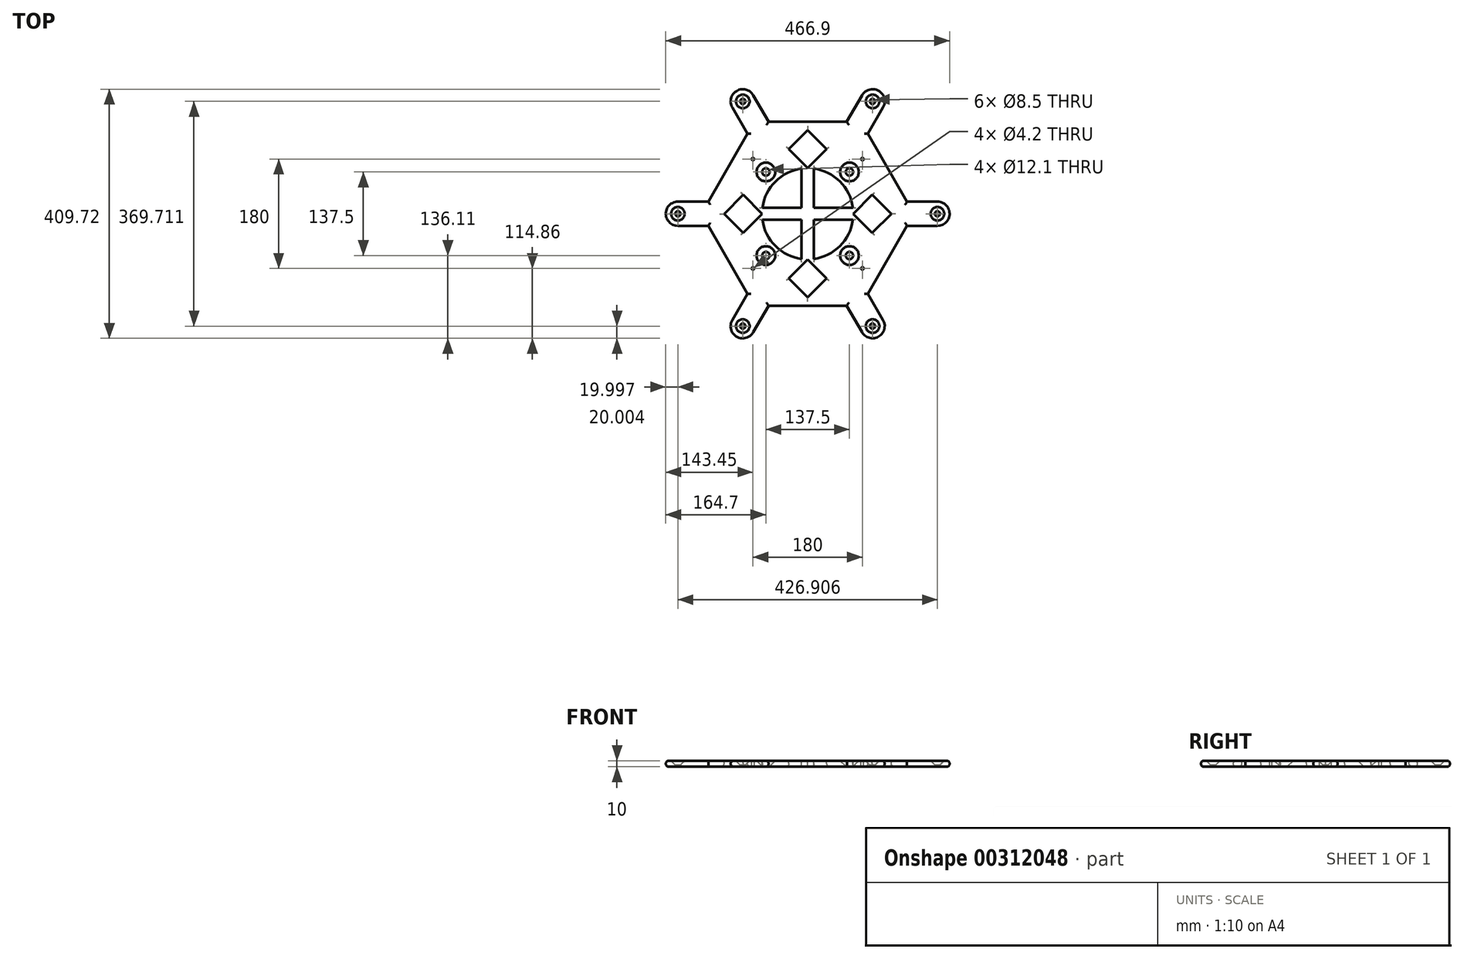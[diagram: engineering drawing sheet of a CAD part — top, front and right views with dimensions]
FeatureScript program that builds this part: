
annotation { "Feature Type Name" : "Feature", "Feature Type Description" : "" }
export const myFeature = defineFeature(function(context is Context, id is Id, definition is map)
    precondition{}
    {
        {
            var Q0;
            Q0=qCreatedBy(makeId("Top.planeOp"),FACE);
            var sketch = newSketch(context, id + "F0", { "sketchPlane" : qUnion([Q0])});
            skCircle(sketch, "E0.cCircle", {"center": v(0, 0) * mm, "radius": 175 * mm, "construction": true});
            skLineSegment(sketch, "E0.0", {"start": v(-87.5, 151.55) * mm, "end": v(87.5, 151.55) * mm});
            skLineSegment(sketch, "E0.1", {"start": v(87.5, 151.55) * mm, "end": v(175, 0) * mm});
            skLineSegment(sketch, "E0.2", {"start": v(175, 0) * mm, "end": v(87.5, -151.55) * mm});
            skLineSegment(sketch, "E0.3", {"start": v(87.5, -151.55) * mm, "end": v(-87.5, -151.55) * mm});
            skLineSegment(sketch, "E0.4", {"start": v(-87.5, -151.55) * mm, "end": v(-175, 0) * mm});
            skLineSegment(sketch, "E0.5", {"start": v(-175, 0) * mm, "end": v(-87.5, 151.55) * mm});
            skLineSegment(sketch, "E1.bottom", {"start": v(-213.45, 20) * mm, "end": v(-163.45, 20) * mm});
            skLineSegment(sketch, "E1.top", {"start": v(-213.45, -20) * mm, "end": v(-163.45, -20) * mm});
            skLineSegment(sketch, "E1.left", {"start": v(-213.45, 20) * mm, "end": v(-213.45, -20) * mm});
            skPoint(sketch, "E2.startSnap0", {"position": v(0, 151.55) * mm});
            skPoint(sketch, "E2.endSnap0", {"position": v(0, -151.55) * mm});
            skLineSegment(sketch, "E3", {"start": v(-175, 0) * mm, "end": v(-213.45, 0) * mm, "construction": true});
            skLineSegment(sketch, "E4.1.0", {"start": v(-124.05, -174.86) * mm, "end": v(-89.4, -194.86) * mm});
            skLineSegment(sketch, "E4.1.1", {"start": v(-124.05, -174.86) * mm, "end": v(-99.05, -131.55) * mm});
            skLineSegment(sketch, "E4.1.2", {"start": v(-89.4, -194.86) * mm, "end": v(-64.4, -151.55) * mm});
            skLineSegment(sketch, "E4.2.0", {"start": v(89.4, -194.86) * mm, "end": v(124.05, -174.86) * mm});
            skLineSegment(sketch, "E4.2.1", {"start": v(89.4, -194.86) * mm, "end": v(64.4, -151.55) * mm});
            skLineSegment(sketch, "E4.2.2", {"start": v(124.05, -174.86) * mm, "end": v(99.05, -131.55) * mm});
            skLineSegment(sketch, "E4.3.0", {"start": v(213.45, -20) * mm, "end": v(213.45, 20) * mm});
            skLineSegment(sketch, "E4.3.1", {"start": v(213.45, -20) * mm, "end": v(163.45, -20) * mm});
            skLineSegment(sketch, "E4.3.2", {"start": v(213.45, 20) * mm, "end": v(163.45, 20) * mm});
            skLineSegment(sketch, "E4.4.0", {"start": v(124.05, 174.86) * mm, "end": v(89.4, 194.86) * mm});
            skLineSegment(sketch, "E4.4.1", {"start": v(124.05, 174.86) * mm, "end": v(99.05, 131.55) * mm});
            skLineSegment(sketch, "E4.4.2", {"start": v(89.4, 194.86) * mm, "end": v(64.4, 151.55) * mm});
            skLineSegment(sketch, "E4.5.0", {"start": v(-89.4, 194.86) * mm, "end": v(-124.05, 174.86) * mm});
            skLineSegment(sketch, "E4.5.1", {"start": v(-89.4, 194.86) * mm, "end": v(-64.4, 151.55) * mm});
            skLineSegment(sketch, "E4.5.2", {"start": v(-124.05, 174.86) * mm, "end": v(-99.05, 131.55) * mm});
            skArc(sketch, "E5", {"start": v(-213.45, 20) * mm, "mid": v(-233.45, 0) * mm, "end": v(-213.45, -20) * mm});
            skArc(sketch, "E6.1.0", {"start": v(-124.05, -174.86) * mm, "mid": v(-116.73, -202.18) * mm, "end": v(-89.4, -194.86) * mm});
            skArc(sketch, "E6.2.0", {"start": v(89.4, -194.86) * mm, "mid": v(116.73, -202.18) * mm, "end": v(124.05, -174.86) * mm});
            skArc(sketch, "E6.3.0", {"start": v(213.45, -20) * mm, "mid": v(233.45, 0) * mm, "end": v(213.45, 20) * mm});
            skArc(sketch, "E6.4.0", {"start": v(124.05, 174.86) * mm, "mid": v(116.73, 202.18) * mm, "end": v(89.4, 194.86) * mm});
            skArc(sketch, "E6.5.0", {"start": v(-89.4, 194.86) * mm, "mid": v(-116.73, 202.18) * mm, "end": v(-124.05, 174.86) * mm});
            skSolve(sketch);
        }
        {
            var Q0;
            Q0 = qSketchRegion(id + "F0", true);
            extrude(context, id + "F1", {"entities" : qUnion([Q0]), "depth" : 10 * mm});
        }
        {
            var Q0;
            Q0=makeQuery(id+"F1.opExtrude","CAP_FACE",FACE,{"disambiguationData":[OSD([sQuery(id+"F0.wireOp",EDGE,"E0.0"),sQuery(id+"F0.wireOp",EDGE,"E0.1"),sQuery(id+"F0.wireOp",EDGE,"E0.2"),sQuery(id+"F0.wireOp",EDGE,"E0.3"),sQuery(id+"F0.wireOp",EDGE,"E0.4"),sQuery(id+"F0.wireOp",EDGE,"E0.5"),sQuery(id+"F0.wireOp",EDGE,"E1.bottom"),sQuery(id+"F0.wireOp",EDGE,"E1.top"),sQuery(id+"F0.wireOp",EDGE,"E4.1.1"),sQuery(id+"F0.wireOp",EDGE,"E4.1.2"),sQuery(id+"F0.wireOp",EDGE,"E4.2.1"),sQuery(id+"F0.wireOp",EDGE,"E4.2.2"),sQuery(id+"F0.wireOp",EDGE,"E4.3.1"),sQuery(id+"F0.wireOp",EDGE,"E4.3.2"),sQuery(id+"F0.wireOp",EDGE,"E4.4.1"),sQuery(id+"F0.wireOp",EDGE,"E4.4.2"),sQuery(id+"F0.wireOp",EDGE,"E4.5.1"),sQuery(id+"F0.wireOp",EDGE,"E4.5.2"),sQuery(id+"F0.wireOp",EDGE,"E5"),sQuery(id+"F0.wireOp",EDGE,"E6.1.0"),sQuery(id+"F0.wireOp",EDGE,"E6.2.0"),sQuery(id+"F0.wireOp",EDGE,"E6.3.0"),sQuery(id+"F0.wireOp",EDGE,"E6.4.0"),sQuery(id+"F0.wireOp",EDGE,"E6.5.0")])],"isStart":false});
            var sketch = newSketch(context, id + "F2", { "sketchPlane" : qUnion([Q0])});
            skCircle(sketch, "E7", {"center": v(0, 0) * mm, "radius": 137.5 * mm});
            skCircle(sketch, "E8", {"center": v(0, 0) * mm, "radius": 75 * mm});
            skLineSegment(sketch, "E9", {"start": v(137.5, 0) * mm, "end": v(0, 137.5) * mm});
            skLineSegment(sketch, "E10", {"start": v(0, 137.5) * mm, "end": v(-137.5, 0) * mm});
            skLineSegment(sketch, "E11", {"start": v(-137.5, 0) * mm, "end": v(0, -137.5) * mm});
            skLineSegment(sketch, "E12", {"start": v(0, -137.5) * mm, "end": v(137.5, 0) * mm});
            skLineSegment(sketch, "E13", {"start": v(-75, 0) * mm, "end": v(-106.25, 31.25) * mm});
            skLineSegment(sketch, "E14", {"start": v(0, 75) * mm, "end": v(-31.25, 106.25) * mm});
            skLineSegment(sketch, "E15", {"start": v(0, 75) * mm, "end": v(31.25, 106.25) * mm});
            skLineSegment(sketch, "E16", {"start": v(-75, 0) * mm, "end": v(-106.25, -31.25) * mm});
            skLineSegment(sketch, "E17", {"start": v(0, -75) * mm, "end": v(-31.25, -106.25) * mm});
            skLineSegment(sketch, "E18", {"start": v(0, -75) * mm, "end": v(31.25, -106.25) * mm});
            skLineSegment(sketch, "E19", {"start": v(75, 0) * mm, "end": v(106.25, 31.25) * mm});
            skLineSegment(sketch, "E20", {"start": v(75, 0) * mm, "end": v(106.25, -31.25) * mm});
            skLineSegment(sketch, "E21", {"start": v(0, 75) * mm, "end": v(0, -75) * mm, "construction": true});
            skLineSegment(sketch, "E22", {"start": v(-75, 0) * mm, "end": v(75, 0) * mm, "construction": true});
            skLineSegment(sketch, "E23", {"start": v(-10, 74.33) * mm, "end": v(-10, -74.33) * mm});
            skLineSegment(sketch, "E24", {"start": v(10, 74.33) * mm, "end": v(10, -74.33) * mm});
            skLineSegment(sketch, "E25", {"start": v(-74.33, 10) * mm, "end": v(74.33, 10) * mm});
            skLineSegment(sketch, "E26", {"start": v(74.33, -10) * mm, "end": v(-74.33, -10) * mm});
            skLineSegment(sketch, "E27", {"start": v(-68.75, 68.75) * mm, "end": v(68.75, -68.75) * mm, "construction": true});
            skLineSegment(sketch, "E28", {"start": v(-68.75, -68.75) * mm, "end": v(68.75, 68.75) * mm, "construction": true});
            skPoint(sketch, "E29", {"position": v(-68.75, 68.75) * mm});
            skPoint(sketch, "E30", {"position": v(68.75, 68.75) * mm});
            skPoint(sketch, "E31", {"position": v(-68.75, -68.75) * mm});
            skPoint(sketch, "E32", {"position": v(68.75, -68.75) * mm});
            skSolve(sketch);
        }
        {
            var Q0;
            {var subQ3=sQuery(id+"F2.wireOp",EDGE,"E13");Q0=makeQuery(id+"F2.imprint","IMPRINT",FACE,{"disambiguationData":[TD([[makeQuery(id+"F2.imprint","IMPRINT",EDGE,{"derivedFrom":subQ3}),1.0]])]});}
            var Q1;
            {var subQ4=sQuery(id+"F2.wireOp",EDGE,"E14");Q1=makeQuery(id+"F2.imprint","IMPRINT",FACE,{"disambiguationData":[TD([[makeQuery(id+"F2.imprint","IMPRINT",EDGE,{"derivedFrom":subQ4}),-1.0]])]});}
            var Q2;
            {var subQ3=sQuery(id+"F2.wireOp",EDGE,"E19");Q2=makeQuery(id+"F2.imprint","IMPRINT",FACE,{"disambiguationData":[TD([[makeQuery(id+"F2.imprint","IMPRINT",EDGE,{"derivedFrom":subQ3}),-1.0]])]});}
            var Q3;
            {var subQ3=sQuery(id+"F2.wireOp",EDGE,"E17");Q3=makeQuery(id+"F2.imprint","IMPRINT",FACE,{"disambiguationData":[TD([[makeQuery(id+"F2.imprint","IMPRINT",EDGE,{"derivedFrom":subQ3}),1.0]])]});}
            var Q4;
            {var subQ0=sQuery(id+"F2.wireOp",EDGE,"E24");var subQ1=sQuery(id+"F2.wireOp",EDGE,"E8");var subQ2=makeQuery(id+"F2.imprint","INTERSECT",VERTEX,{"disambiguationData":[OD(1.0)],"derivedFrom":[subQ1,subQ0]});Q4=makeQuery(id+"F2.imprint","IMPRINT",FACE,{"disambiguationData":[TD([[makeQuery(id+"F2.imprint","IMPRINT",EDGE,{"disambiguationData":[TD([[subQ2,-1.0]])],"derivedFrom":subQ1}),1.0]])]});}
            var Q5;
            {var subQ0=sQuery(id+"F2.wireOp",EDGE,"E23");var subQ1=sQuery(id+"F2.wireOp",EDGE,"E8");var subQ2=makeQuery(id+"F2.imprint","INTERSECT",VERTEX,{"disambiguationData":[OD(1.0)],"derivedFrom":[subQ1,subQ0]});Q5=makeQuery(id+"F2.imprint","IMPRINT",FACE,{"disambiguationData":[TD([[makeQuery(id+"F2.imprint","IMPRINT",EDGE,{"disambiguationData":[TD([[subQ2,1.0]])],"derivedFrom":subQ1}),1.0]])]});}
            var Q6;
            {var subQ0=sQuery(id+"F2.wireOp",EDGE,"E23");var subQ1=sQuery(id+"F2.wireOp",EDGE,"E8");var subQ2=makeQuery(id+"F2.imprint","INTERSECT",VERTEX,{"disambiguationData":[OD(0.0)],"derivedFrom":[subQ1,subQ0]});Q6=makeQuery(id+"F2.imprint","IMPRINT",FACE,{"disambiguationData":[TD([[makeQuery(id+"F2.imprint","IMPRINT",EDGE,{"disambiguationData":[TD([[subQ2,-1.0]])],"derivedFrom":subQ1}),1.0]])]});}
            var Q7;
            {var subQ0=sQuery(id+"F2.wireOp",EDGE,"E24");var subQ1=sQuery(id+"F2.wireOp",EDGE,"E8");var subQ2=makeQuery(id+"F2.imprint","INTERSECT",VERTEX,{"disambiguationData":[OD(0.0)],"derivedFrom":[subQ1,subQ0]});Q7=makeQuery(id+"F2.imprint","IMPRINT",FACE,{"disambiguationData":[TD([[makeQuery(id+"F2.imprint","IMPRINT",EDGE,{"disambiguationData":[TD([[subQ2,1.0]])],"derivedFrom":subQ1}),1.0]])]});}
            extrude(context, id + "F3", {"entities" : qUnion([Q0, Q1, Q2, Q3, Q4, Q5, Q6, Q7]), "operationType" : NewBodyOperationType.REMOVE, "endBound" : BoundingType.THROUGH_ALL, "oppositeDirection" : true, "depth" : 25 * mm});
        }
        {
            var Q0;
            Q0=makeQuery(id+"F1.opExtrude","CAP_FACE",FACE,{"disambiguationData":[OSD([sQuery(id+"F0.wireOp",EDGE,"E0.0"),sQuery(id+"F0.wireOp",EDGE,"E0.1"),sQuery(id+"F0.wireOp",EDGE,"E0.2"),sQuery(id+"F0.wireOp",EDGE,"E0.3"),sQuery(id+"F0.wireOp",EDGE,"E0.4"),sQuery(id+"F0.wireOp",EDGE,"E0.5"),sQuery(id+"F0.wireOp",EDGE,"E1.bottom"),sQuery(id+"F0.wireOp",EDGE,"E1.top"),sQuery(id+"F0.wireOp",EDGE,"E4.1.1"),sQuery(id+"F0.wireOp",EDGE,"E4.1.2"),sQuery(id+"F0.wireOp",EDGE,"E4.2.1"),sQuery(id+"F0.wireOp",EDGE,"E4.2.2"),sQuery(id+"F0.wireOp",EDGE,"E4.3.1"),sQuery(id+"F0.wireOp",EDGE,"E4.3.2"),sQuery(id+"F0.wireOp",EDGE,"E4.4.1"),sQuery(id+"F0.wireOp",EDGE,"E4.4.2"),sQuery(id+"F0.wireOp",EDGE,"E4.5.1"),sQuery(id+"F0.wireOp",EDGE,"E4.5.2"),sQuery(id+"F0.wireOp",EDGE,"E5"),sQuery(id+"F0.wireOp",EDGE,"E6.1.0"),sQuery(id+"F0.wireOp",EDGE,"E6.2.0"),sQuery(id+"F0.wireOp",EDGE,"E6.3.0"),sQuery(id+"F0.wireOp",EDGE,"E6.4.0"),sQuery(id+"F0.wireOp",EDGE,"E6.5.0")])],"isStart":false});
            var sketch = newSketch(context, id + "F4", { "sketchPlane" : qUnion([Q0])});
            skPoint(sketch, "E33", {"position": v(-213.45, 0) * mm});
            skPoint(sketch, "E34.1.0", {"position": v(-106.73, -184.86) * mm});
            skPoint(sketch, "E34.2.0", {"position": v(106.73, -184.86) * mm});
            skPoint(sketch, "E34.3.0", {"position": v(213.45, 0) * mm});
            skPoint(sketch, "E34.4.0", {"position": v(106.73, 184.86) * mm});
            skPoint(sketch, "E34.5.0", {"position": v(-106.73, 184.86) * mm});
            skPoint(sketch, "E34.center", {"position": v(0, 0) * mm});
            skSolve(sketch);
        }
        {
            var Q0;
            Q0=sQuery(id+"F4.wireOp",VERTEX,"E33");
            var Q1;
            Q1=sQuery(id+"F4.wireOp",VERTEX,"E34.5.0");
            var Q2;
            Q2=sQuery(id+"F4.wireOp",VERTEX,"E34.4.0");
            var Q3;
            Q3=sQuery(id+"F4.wireOp",VERTEX,"E34.3.0");
            var Q4;
            Q4=sQuery(id+"F4.wireOp",VERTEX,"E34.2.0");
            var Q5;
            Q5=sQuery(id+"F4.wireOp",VERTEX,"E34.1.0");
            var Q6;
            Q6=makeQuery(id+"F1.opExtrude","SWEPT_BODY",BODY,{"disambiguationData":[OSD([sQuery(id+"F0.wireOp",EDGE,"E0.0"),sQuery(id+"F0.wireOp",EDGE,"E0.1"),sQuery(id+"F0.wireOp",EDGE,"E0.2"),sQuery(id+"F0.wireOp",EDGE,"E0.3"),sQuery(id+"F0.wireOp",EDGE,"E0.4"),sQuery(id+"F0.wireOp",EDGE,"E0.5"),sQuery(id+"F0.wireOp",EDGE,"E1.bottom"),sQuery(id+"F0.wireOp",EDGE,"E1.top"),sQuery(id+"F0.wireOp",EDGE,"E4.1.1"),sQuery(id+"F0.wireOp",EDGE,"E4.1.2"),sQuery(id+"F0.wireOp",EDGE,"E4.2.1"),sQuery(id+"F0.wireOp",EDGE,"E4.2.2"),sQuery(id+"F0.wireOp",EDGE,"E4.3.1"),sQuery(id+"F0.wireOp",EDGE,"E4.3.2"),sQuery(id+"F0.wireOp",EDGE,"E4.4.1"),sQuery(id+"F0.wireOp",EDGE,"E4.4.2"),sQuery(id+"F0.wireOp",EDGE,"E4.5.1"),sQuery(id+"F0.wireOp",EDGE,"E4.5.2"),sQuery(id+"F0.wireOp",EDGE,"E5"),sQuery(id+"F0.wireOp",EDGE,"E6.1.0"),sQuery(id+"F0.wireOp",EDGE,"E6.2.0"),sQuery(id+"F0.wireOp",EDGE,"E6.3.0"),sQuery(id+"F0.wireOp",EDGE,"E6.4.0"),sQuery(id+"F0.wireOp",EDGE,"E6.5.0")])]});
            hole(context, id + "F5", {"style" : HoleStyle.C_SINK, "endStyle" : HoleEndStyle.THROUGH, "standardTappedOrClearance" : lookupTablePath({ "standard" : "ISO", "engagement" : "75%", "pitch" : "1.5 mm", "size" : "M10", "type" : "Tapped" }), "standardBlindInLast" : lookupTablePath({ "standard" : "ISO", "engagement" : "75%", "pitch" : "1.5 mm", "size" : "M10", "type" : "Tapped" }), "holeDiameter" : 8.5 * mm, "cSinkDiameter" : 22.4 * mm, "cSinkAngle" : 90 * degree, "showTappedDepth" : true, "tappedDepth" : 6 * mm, "tapClearance" : 3, "locations" : qUnion([Q0, Q1, Q2, Q3, Q4, Q5]), "scope" : qUnion([Q6]), "majorDiameter" : 10 * mm});
        }
        {
            var Q0;
            Q0=makeQuery(id+"F1.opExtrude","CAP_FACE",FACE,{"disambiguationData":[OSD([sQuery(id+"F0.wireOp",EDGE,"E0.0"),sQuery(id+"F0.wireOp",EDGE,"E0.1"),sQuery(id+"F0.wireOp",EDGE,"E0.2"),sQuery(id+"F0.wireOp",EDGE,"E0.3"),sQuery(id+"F0.wireOp",EDGE,"E0.4"),sQuery(id+"F0.wireOp",EDGE,"E0.5"),sQuery(id+"F0.wireOp",EDGE,"E1.bottom"),sQuery(id+"F0.wireOp",EDGE,"E1.top"),sQuery(id+"F0.wireOp",EDGE,"E4.1.1"),sQuery(id+"F0.wireOp",EDGE,"E4.1.2"),sQuery(id+"F0.wireOp",EDGE,"E4.2.1"),sQuery(id+"F0.wireOp",EDGE,"E4.2.2"),sQuery(id+"F0.wireOp",EDGE,"E4.3.1"),sQuery(id+"F0.wireOp",EDGE,"E4.3.2"),sQuery(id+"F0.wireOp",EDGE,"E4.4.1"),sQuery(id+"F0.wireOp",EDGE,"E4.4.2"),sQuery(id+"F0.wireOp",EDGE,"E4.5.1"),sQuery(id+"F0.wireOp",EDGE,"E4.5.2"),sQuery(id+"F0.wireOp",EDGE,"E5"),sQuery(id+"F0.wireOp",EDGE,"E6.1.0"),sQuery(id+"F0.wireOp",EDGE,"E6.2.0"),sQuery(id+"F0.wireOp",EDGE,"E6.3.0"),sQuery(id+"F0.wireOp",EDGE,"E6.4.0"),sQuery(id+"F0.wireOp",EDGE,"E6.5.0")])],"isStart":false});
            var sketch = newSketch(context, id + "F6", { "sketchPlane" : qUnion([Q0])});
            skLineSegment(sketch, "E35.bottom", {"start": v(-100, 100) * mm, "end": v(100, 100) * mm, "construction": true});
            skLineSegment(sketch, "E35.top", {"start": v(-100, -100) * mm, "end": v(100, -100) * mm, "construction": true});
            skLineSegment(sketch, "E35.left", {"start": v(-100, 100) * mm, "end": v(-100, -100) * mm, "construction": true});
            skLineSegment(sketch, "E35.right", {"start": v(100, 100) * mm, "end": v(100, -100) * mm, "construction": true});
            skPoint(sketch, "E35.middle", {"position": v(0, 0) * mm});
            skSolve(sketch);
        }
        {
            var Q0;
            Q0=makeQuery(id+"F6.imprint","IMPRINT",FACE,{"disambiguationData":[TD([[makeQuery(id+"F6.imprint","IMPRINT",EDGE,{"derivedFrom":makeQuery(id+"F1.opExtrude","CAP_EDGE",EDGE,{"disambiguationData":[OSD([sQuery(id+"F0.wireOp",EDGE,"E0.0")])],"isStart":false})}),-1.0]])]});
            var sketch = newSketch(context, id + "F7", { "sketchPlane" : qUnion([Q0])});
            skLineSegment(sketch, "E36.bottom", {"start": v(-90, 90) * mm, "end": v(90, 90) * mm, "construction": true});
            skLineSegment(sketch, "E36.top", {"start": v(-90, -90) * mm, "end": v(90, -90) * mm, "construction": true});
            skLineSegment(sketch, "E36.left", {"start": v(-90, 90) * mm, "end": v(-90, -90) * mm, "construction": true});
            skLineSegment(sketch, "E36.right", {"start": v(90, 90) * mm, "end": v(90, -90) * mm, "construction": true});
            skPoint(sketch, "E36.middle", {"position": v(0, 0) * mm});
            skPoint(sketch, "E37", {"position": v(-90, 90) * mm});
            skPoint(sketch, "E38", {"position": v(90, 90) * mm});
            skPoint(sketch, "E39", {"position": v(90, -90) * mm});
            skPoint(sketch, "E40", {"position": v(-90, -90) * mm});
            skSolve(sketch);
        }
        {
            var Q0;
            Q0=sQuery(id+"F7.wireOp",VERTEX,"E37");
            var Q1;
            Q1=sQuery(id+"F7.wireOp",VERTEX,"E38");
            var Q2;
            Q2=sQuery(id+"F7.wireOp",VERTEX,"E39");
            var Q3;
            Q3=sQuery(id+"F7.wireOp",VERTEX,"E40");
            var Q4;
            Q4=makeQuery(id+"F1.opExtrude","SWEPT_BODY",BODY,{"disambiguationData":[OSD([sQuery(id+"F0.wireOp",EDGE,"E0.0"),sQuery(id+"F0.wireOp",EDGE,"E0.1"),sQuery(id+"F0.wireOp",EDGE,"E0.2"),sQuery(id+"F0.wireOp",EDGE,"E0.3"),sQuery(id+"F0.wireOp",EDGE,"E0.4"),sQuery(id+"F0.wireOp",EDGE,"E0.5"),sQuery(id+"F0.wireOp",EDGE,"E1.bottom"),sQuery(id+"F0.wireOp",EDGE,"E1.top"),sQuery(id+"F0.wireOp",EDGE,"E4.1.1"),sQuery(id+"F0.wireOp",EDGE,"E4.1.2"),sQuery(id+"F0.wireOp",EDGE,"E4.2.1"),sQuery(id+"F0.wireOp",EDGE,"E4.2.2"),sQuery(id+"F0.wireOp",EDGE,"E4.3.1"),sQuery(id+"F0.wireOp",EDGE,"E4.3.2"),sQuery(id+"F0.wireOp",EDGE,"E4.4.1"),sQuery(id+"F0.wireOp",EDGE,"E4.4.2"),sQuery(id+"F0.wireOp",EDGE,"E4.5.1"),sQuery(id+"F0.wireOp",EDGE,"E4.5.2"),sQuery(id+"F0.wireOp",EDGE,"E5"),sQuery(id+"F0.wireOp",EDGE,"E6.1.0"),sQuery(id+"F0.wireOp",EDGE,"E6.2.0"),sQuery(id+"F0.wireOp",EDGE,"E6.3.0"),sQuery(id+"F0.wireOp",EDGE,"E6.4.0"),sQuery(id+"F0.wireOp",EDGE,"E6.5.0")])]});
            hole(context, id + "F8", {"style" : HoleStyle.SIMPLE, "endStyle" : HoleEndStyle.THROUGH, "standardTappedOrClearance" : lookupTablePath({ "standard" : "ISO", "engagement" : "75%", "pitch" : "0.8 mm", "size" : "M5", "type" : "Tapped" }), "standardBlindInLast" : lookupTablePath({ "standard" : "ISO", "engagement" : "75%", "pitch" : "0.8 mm", "size" : "M5", "type" : "Tapped" }), "holeDiameter" : 4.2 * mm, "showTappedDepth" : true, "tappedDepth" : 6 * mm, "tapClearance" : 3, "locations" : qUnion([Q0, Q1, Q2, Q3]), "scope" : qUnion([Q4]), "majorDiameter" : 5 * mm});
        }
        {
            var Q0;
            Q0=sQuery(id+"F2.wireOp",VERTEX,"E29");
            var Q1;
            Q1=sQuery(id+"F2.wireOp",VERTEX,"E30");
            var Q2;
            Q2=sQuery(id+"F2.wireOp",VERTEX,"E32");
            var Q3;
            Q3=sQuery(id+"F2.wireOp",VERTEX,"E31");
            var Q4;
            Q4=makeQuery(id+"F1.opExtrude","SWEPT_BODY",BODY,{"disambiguationData":[OSD([sQuery(id+"F0.wireOp",EDGE,"E0.0"),sQuery(id+"F0.wireOp",EDGE,"E0.1"),sQuery(id+"F0.wireOp",EDGE,"E0.2"),sQuery(id+"F0.wireOp",EDGE,"E0.3"),sQuery(id+"F0.wireOp",EDGE,"E0.4"),sQuery(id+"F0.wireOp",EDGE,"E0.5"),sQuery(id+"F0.wireOp",EDGE,"E1.bottom"),sQuery(id+"F0.wireOp",EDGE,"E1.top"),sQuery(id+"F0.wireOp",EDGE,"E4.1.1"),sQuery(id+"F0.wireOp",EDGE,"E4.1.2"),sQuery(id+"F0.wireOp",EDGE,"E4.2.1"),sQuery(id+"F0.wireOp",EDGE,"E4.2.2"),sQuery(id+"F0.wireOp",EDGE,"E4.3.1"),sQuery(id+"F0.wireOp",EDGE,"E4.3.2"),sQuery(id+"F0.wireOp",EDGE,"E4.4.1"),sQuery(id+"F0.wireOp",EDGE,"E4.4.2"),sQuery(id+"F0.wireOp",EDGE,"E4.5.1"),sQuery(id+"F0.wireOp",EDGE,"E4.5.2"),sQuery(id+"F0.wireOp",EDGE,"E5"),sQuery(id+"F0.wireOp",EDGE,"E6.1.0"),sQuery(id+"F0.wireOp",EDGE,"E6.2.0"),sQuery(id+"F0.wireOp",EDGE,"E6.3.0"),sQuery(id+"F0.wireOp",EDGE,"E6.4.0"),sQuery(id+"F0.wireOp",EDGE,"E6.5.0")])]});
            hole(context, id + "F9", {"style" : HoleStyle.C_SINK, "endStyle" : HoleEndStyle.THROUGH, "standardTappedOrClearance" : lookupTablePath({ "standard" : "ISO", "engagement" : "75%", "pitch" : "2 mm", "size" : "M14", "type" : "Tapped" }), "standardBlindInLast" : lookupTablePath({ "standard" : "ISO", "engagement" : "75%", "pitch" : "2 mm", "size" : "M14", "type" : "Tapped" }), "holeDiameter" : 12.1 * mm, "cSinkDiameter" : 30.8 * mm, "cSinkAngle" : 90 * degree, "showTappedDepth" : true, "tappedDepth" : 6 * mm, "tapClearance" : 3, "locations" : qUnion([Q0, Q1, Q2, Q3]), "scope" : qUnion([Q4]), "majorDiameter" : 14 * mm});
        }
        {
            var Q0;
            Q0=makeQuery(id+"F1.opExtrude","CAP_EDGE",EDGE,{"disambiguationData":[OSD([sQuery(id+"F0.wireOp",EDGE,"E4.5.1")])],"isStart":false});
            var Q1;
            Q1=makeQuery(id+"F1.opExtrude","CAP_EDGE",EDGE,{"disambiguationData":[OSD([sQuery(id+"F0.wireOp",EDGE,"E0.0")])],"isStart":false});
            var Q2;
            Q2=makeQuery(id+"F1.opExtrude","CAP_EDGE",EDGE,{"disambiguationData":[OSD([sQuery(id+"F0.wireOp",EDGE,"E4.4.2")])],"isStart":false});
            var Q3;
            Q3=makeQuery(id+"F1.opExtrude","CAP_EDGE",EDGE,{"disambiguationData":[OSD([sQuery(id+"F0.wireOp",EDGE,"E6.4.0")])],"isStart":false});
            var Q4;
            Q4=makeQuery(id+"F1.opExtrude","CAP_EDGE",EDGE,{"disambiguationData":[OSD([sQuery(id+"F0.wireOp",EDGE,"E4.4.1")])],"isStart":false});
            var Q5;
            Q5=makeQuery(id+"F1.opExtrude","CAP_EDGE",EDGE,{"disambiguationData":[OSD([sQuery(id+"F0.wireOp",EDGE,"E0.1")])],"isStart":false});
            var Q6;
            Q6=makeQuery(id+"F1.opExtrude","CAP_EDGE",EDGE,{"disambiguationData":[OSD([sQuery(id+"F0.wireOp",EDGE,"E4.3.2")])],"isStart":false});
            var Q7;
            Q7=makeQuery(id+"F1.opExtrude","CAP_EDGE",EDGE,{"disambiguationData":[OSD([sQuery(id+"F0.wireOp",EDGE,"E6.3.0")])],"isStart":false});
            var Q8;
            Q8=makeQuery(id+"F1.opExtrude","CAP_EDGE",EDGE,{"disambiguationData":[OSD([sQuery(id+"F0.wireOp",EDGE,"E4.3.1")])],"isStart":false});
            var Q9;
            Q9=makeQuery(id+"F1.opExtrude","CAP_EDGE",EDGE,{"disambiguationData":[OSD([sQuery(id+"F0.wireOp",EDGE,"E0.2")])],"isStart":false});
            var Q10;
            Q10=makeQuery(id+"F1.opExtrude","CAP_EDGE",EDGE,{"disambiguationData":[OSD([sQuery(id+"F0.wireOp",EDGE,"E4.2.2")])],"isStart":false});
            var Q11;
            Q11=makeQuery(id+"F1.opExtrude","CAP_EDGE",EDGE,{"disambiguationData":[OSD([sQuery(id+"F0.wireOp",EDGE,"E6.2.0")])],"isStart":false});
            var Q12;
            Q12=makeQuery(id+"F1.opExtrude","CAP_EDGE",EDGE,{"disambiguationData":[OSD([sQuery(id+"F0.wireOp",EDGE,"E4.2.1")])],"isStart":false});
            var Q13;
            Q13=makeQuery(id+"F1.opExtrude","CAP_EDGE",EDGE,{"disambiguationData":[OSD([sQuery(id+"F0.wireOp",EDGE,"E0.3")])],"isStart":false});
            var Q14;
            Q14=makeQuery(id+"F1.opExtrude","CAP_EDGE",EDGE,{"disambiguationData":[OSD([sQuery(id+"F0.wireOp",EDGE,"E4.1.2")])],"isStart":false});
            var Q15;
            Q15=makeQuery(id+"F1.opExtrude","CAP_EDGE",EDGE,{"disambiguationData":[OSD([sQuery(id+"F0.wireOp",EDGE,"E6.1.0")])],"isStart":false});
            var Q16;
            Q16=makeQuery(id+"F1.opExtrude","CAP_EDGE",EDGE,{"disambiguationData":[OSD([sQuery(id+"F0.wireOp",EDGE,"E4.1.1")])],"isStart":false});
            var Q17;
            Q17=makeQuery(id+"F1.opExtrude","CAP_EDGE",EDGE,{"disambiguationData":[OSD([sQuery(id+"F0.wireOp",EDGE,"E0.4")])],"isStart":false});
            var Q18;
            Q18=makeQuery(id+"F1.opExtrude","CAP_EDGE",EDGE,{"disambiguationData":[OSD([sQuery(id+"F0.wireOp",EDGE,"E1.top")])],"isStart":false});
            var Q19;
            Q19=makeQuery(id+"F1.opExtrude","CAP_EDGE",EDGE,{"disambiguationData":[OSD([sQuery(id+"F0.wireOp",EDGE,"E5")])],"isStart":false});
            var Q20;
            Q20=makeQuery(id+"F1.opExtrude","CAP_EDGE",EDGE,{"disambiguationData":[OSD([sQuery(id+"F0.wireOp",EDGE,"E1.bottom")])],"isStart":false});
            var Q21;
            Q21=makeQuery(id+"F1.opExtrude","CAP_EDGE",EDGE,{"disambiguationData":[OSD([sQuery(id+"F0.wireOp",EDGE,"E0.5")])],"isStart":false});
            var Q22;
            Q22=makeQuery(id+"F1.opExtrude","CAP_EDGE",EDGE,{"disambiguationData":[OSD([sQuery(id+"F0.wireOp",EDGE,"E4.5.2")])],"isStart":false});
            var Q23;
            Q23=makeQuery(id+"F1.opExtrude","CAP_EDGE",EDGE,{"disambiguationData":[OSD([sQuery(id+"F0.wireOp",EDGE,"E6.5.0")])],"isStart":false});
            var Q24;
            {var subQ0=sQuery(id+"F2.wireOp",EDGE,"E10");Q24=makeQuery(id+"F3.boolean.opBoolean","COPY",EDGE,{"derivedFrom":makeQuery(id+"F3.opExtrude","CAP_EDGE",EDGE,{"disambiguationData":[OSD([subQ0]),TDD([makeQuery(id+"F2.imprint","IMPRINT",EDGE,{"disambiguationData":[TD([[makeQuery(id+"F2.imprint","INTERSECT",VERTEX,{"derivedFrom":[subQ0,sQuery(id+"F2.wireOp",EDGE,"E14")]}),1.0]])],"derivedFrom":subQ0})])],"isStart":true})});}
            var Q25;
            {var subQ0=sQuery(id+"F2.wireOp",EDGE,"E9");Q25=makeQuery(id+"F3.boolean.opBoolean","COPY",EDGE,{"derivedFrom":makeQuery(id+"F3.opExtrude","CAP_EDGE",EDGE,{"disambiguationData":[OSD([subQ0]),TDD([makeQuery(id+"F2.imprint","IMPRINT",EDGE,{"disambiguationData":[TD([[makeQuery(id+"F2.imprint","INTERSECT",VERTEX,{"derivedFrom":[subQ0,sQuery(id+"F2.wireOp",EDGE,"E15")]}),-1.0]])],"derivedFrom":subQ0})])],"isStart":true})});}
            var Q26;
            {var subQ0=sQuery(id+"F2.wireOp",EDGE,"E11");Q26=makeQuery(id+"F3.boolean.opBoolean","COPY",EDGE,{"derivedFrom":makeQuery(id+"F3.opExtrude","CAP_EDGE",EDGE,{"disambiguationData":[OSD([subQ0]),TDD([makeQuery(id+"F2.imprint","IMPRINT",EDGE,{"disambiguationData":[TD([[makeQuery(id+"F2.imprint","INTERSECT",VERTEX,{"derivedFrom":[subQ0,sQuery(id+"F2.wireOp",EDGE,"E16")]}),1.0]])],"derivedFrom":subQ0})])],"isStart":true})});}
            var Q27;
            {var subQ0=sQuery(id+"F2.wireOp",EDGE,"E8");Q27=makeQuery(id+"F3.boolean.opBoolean","COPY",EDGE,{"derivedFrom":makeQuery(id+"F3.opExtrude","CAP_EDGE",EDGE,{"disambiguationData":[OSD([subQ0]),TDD([makeQuery(id+"F2.imprint","IMPRINT",EDGE,{"disambiguationData":[TD([[makeQuery(id+"F2.imprint","INTERSECT",VERTEX,{"disambiguationData":[OD(0.0)],"derivedFrom":[subQ0,sQuery(id+"F2.wireOp",EDGE,"E23")]}),-1.0]])],"derivedFrom":subQ0})])],"isStart":true})});}
            var Q28;
            {var subQ0=sQuery(id+"F2.wireOp",EDGE,"E8");Q28=makeQuery(id+"F3.boolean.opBoolean","COPY",EDGE,{"derivedFrom":makeQuery(id+"F3.opExtrude","CAP_EDGE",EDGE,{"disambiguationData":[OSD([subQ0]),TDD([makeQuery(id+"F2.imprint","IMPRINT",EDGE,{"disambiguationData":[TD([[makeQuery(id+"F2.imprint","INTERSECT",VERTEX,{"disambiguationData":[OD(0.0)],"derivedFrom":[subQ0,sQuery(id+"F2.wireOp",EDGE,"E24")]}),1.0]])],"derivedFrom":subQ0})])],"isStart":true})});}
            var Q29;
            {var subQ0=sQuery(id+"F2.wireOp",EDGE,"E8");Q29=makeQuery(id+"F3.boolean.opBoolean","COPY",EDGE,{"derivedFrom":makeQuery(id+"F3.opExtrude","CAP_EDGE",EDGE,{"disambiguationData":[OSD([subQ0]),TDD([makeQuery(id+"F2.imprint","IMPRINT",EDGE,{"disambiguationData":[TD([[makeQuery(id+"F2.imprint","INTERSECT",VERTEX,{"disambiguationData":[OD(1.0)],"derivedFrom":[subQ0,sQuery(id+"F2.wireOp",EDGE,"E24")]}),-1.0]])],"derivedFrom":subQ0})])],"isStart":true})});}
            var Q30;
            {var subQ0=sQuery(id+"F2.wireOp",EDGE,"E8");Q30=makeQuery(id+"F3.boolean.opBoolean","COPY",EDGE,{"derivedFrom":makeQuery(id+"F3.opExtrude","CAP_EDGE",EDGE,{"disambiguationData":[OSD([subQ0]),TDD([makeQuery(id+"F2.imprint","IMPRINT",EDGE,{"disambiguationData":[TD([[makeQuery(id+"F2.imprint","INTERSECT",VERTEX,{"disambiguationData":[OD(1.0)],"derivedFrom":[subQ0,sQuery(id+"F2.wireOp",EDGE,"E23")]}),1.0]])],"derivedFrom":subQ0})])],"isStart":true})});}
            var Q31;
            {var subQ0=sQuery(id+"F2.wireOp",EDGE,"E9");Q31=makeQuery(id+"F3.boolean.opBoolean","COPY",EDGE,{"derivedFrom":makeQuery(id+"F3.opExtrude","CAP_EDGE",EDGE,{"disambiguationData":[OSD([subQ0]),TDD([makeQuery(id+"F2.imprint","IMPRINT",EDGE,{"disambiguationData":[TD([[makeQuery(id+"F2.imprint","INTERSECT",VERTEX,{"derivedFrom":[subQ0,sQuery(id+"F2.wireOp",EDGE,"E19")]}),1.0]])],"derivedFrom":subQ0})])],"isStart":true})});}
            var Q32;
            {var subQ0=sQuery(id+"F2.wireOp",EDGE,"E12");Q32=makeQuery(id+"F3.boolean.opBoolean","COPY",EDGE,{"derivedFrom":makeQuery(id+"F3.opExtrude","CAP_EDGE",EDGE,{"disambiguationData":[OSD([subQ0]),TDD([makeQuery(id+"F2.imprint","IMPRINT",EDGE,{"disambiguationData":[TD([[makeQuery(id+"F2.imprint","INTERSECT",VERTEX,{"derivedFrom":[subQ0,sQuery(id+"F2.wireOp",EDGE,"E20")]}),-1.0]])],"derivedFrom":subQ0})])],"isStart":true})});}
            var Q33;
            {var subQ0=sQuery(id+"F2.wireOp",EDGE,"E11");Q33=makeQuery(id+"F3.boolean.opBoolean","COPY",EDGE,{"derivedFrom":makeQuery(id+"F3.opExtrude","CAP_EDGE",EDGE,{"disambiguationData":[OSD([subQ0]),TDD([makeQuery(id+"F2.imprint","IMPRINT",EDGE,{"disambiguationData":[TD([[makeQuery(id+"F2.imprint","INTERSECT",VERTEX,{"derivedFrom":[subQ0,sQuery(id+"F2.wireOp",EDGE,"E17")]}),-1.0]])],"derivedFrom":subQ0})])],"isStart":true})});}
            var Q34;
            {var subQ0=sQuery(id+"F2.wireOp",EDGE,"E12");Q34=makeQuery(id+"F3.boolean.opBoolean","COPY",EDGE,{"derivedFrom":makeQuery(id+"F3.opExtrude","CAP_EDGE",EDGE,{"disambiguationData":[OSD([subQ0]),TDD([makeQuery(id+"F2.imprint","IMPRINT",EDGE,{"disambiguationData":[TD([[makeQuery(id+"F2.imprint","INTERSECT",VERTEX,{"derivedFrom":[subQ0,sQuery(id+"F2.wireOp",EDGE,"E18")]}),1.0]])],"derivedFrom":subQ0})])],"isStart":true})});}
            var Q35;
            Q35=makeQuery(id+"F1.opExtrude","CAP_EDGE",EDGE,{"disambiguationData":[OSD([sQuery(id+"F0.wireOp",EDGE,"E4.2.2")])],"isStart":true});
            var Q36;
            Q36=makeQuery(id+"F1.opExtrude","CAP_EDGE",EDGE,{"disambiguationData":[OSD([sQuery(id+"F0.wireOp",EDGE,"E6.2.0")])],"isStart":true});
            var Q37;
            Q37=makeQuery(id+"F1.opExtrude","CAP_EDGE",EDGE,{"disambiguationData":[OSD([sQuery(id+"F0.wireOp",EDGE,"E4.2.1")])],"isStart":true});
            var Q38;
            Q38=makeQuery(id+"F1.opExtrude","CAP_EDGE",EDGE,{"disambiguationData":[OSD([sQuery(id+"F0.wireOp",EDGE,"E0.3")])],"isStart":true});
            var Q39;
            Q39=makeQuery(id+"F1.opExtrude","CAP_EDGE",EDGE,{"disambiguationData":[OSD([sQuery(id+"F0.wireOp",EDGE,"E4.1.2")])],"isStart":true});
            var Q40;
            Q40=makeQuery(id+"F1.opExtrude","CAP_EDGE",EDGE,{"disambiguationData":[OSD([sQuery(id+"F0.wireOp",EDGE,"E6.1.0")])],"isStart":true});
            var Q41;
            Q41=makeQuery(id+"F1.opExtrude","CAP_EDGE",EDGE,{"disambiguationData":[OSD([sQuery(id+"F0.wireOp",EDGE,"E4.1.1")])],"isStart":true});
            var Q42;
            Q42=makeQuery(id+"F1.opExtrude","CAP_EDGE",EDGE,{"disambiguationData":[OSD([sQuery(id+"F0.wireOp",EDGE,"E0.4")])],"isStart":true});
            var Q43;
            Q43=makeQuery(id+"F1.opExtrude","CAP_EDGE",EDGE,{"disambiguationData":[OSD([sQuery(id+"F0.wireOp",EDGE,"E1.top")])],"isStart":true});
            var Q44;
            Q44=makeQuery(id+"F1.opExtrude","CAP_EDGE",EDGE,{"disambiguationData":[OSD([sQuery(id+"F0.wireOp",EDGE,"E5")])],"isStart":true});
            var Q45;
            Q45=makeQuery(id+"F1.opExtrude","CAP_EDGE",EDGE,{"disambiguationData":[OSD([sQuery(id+"F0.wireOp",EDGE,"E1.bottom")])],"isStart":true});
            var Q46;
            Q46=makeQuery(id+"F1.opExtrude","CAP_EDGE",EDGE,{"disambiguationData":[OSD([sQuery(id+"F0.wireOp",EDGE,"E0.5")])],"isStart":true});
            var Q47;
            Q47=makeQuery(id+"F1.opExtrude","CAP_EDGE",EDGE,{"disambiguationData":[OSD([sQuery(id+"F0.wireOp",EDGE,"E4.5.2")])],"isStart":true});
            var Q48;
            Q48=makeQuery(id+"F1.opExtrude","CAP_EDGE",EDGE,{"disambiguationData":[OSD([sQuery(id+"F0.wireOp",EDGE,"E6.5.0")])],"isStart":true});
            var Q49;
            Q49=makeQuery(id+"F1.opExtrude","CAP_EDGE",EDGE,{"disambiguationData":[OSD([sQuery(id+"F0.wireOp",EDGE,"E4.5.1")])],"isStart":true});
            var Q50;
            Q50=makeQuery(id+"F1.opExtrude","CAP_EDGE",EDGE,{"disambiguationData":[OSD([sQuery(id+"F0.wireOp",EDGE,"E0.0")])],"isStart":true});
            var Q51;
            Q51=makeQuery(id+"F1.opExtrude","CAP_EDGE",EDGE,{"disambiguationData":[OSD([sQuery(id+"F0.wireOp",EDGE,"E4.4.2")])],"isStart":true});
            var Q52;
            Q52=makeQuery(id+"F1.opExtrude","CAP_EDGE",EDGE,{"disambiguationData":[OSD([sQuery(id+"F0.wireOp",EDGE,"E6.4.0")])],"isStart":true});
            var Q53;
            Q53=makeQuery(id+"F1.opExtrude","CAP_EDGE",EDGE,{"disambiguationData":[OSD([sQuery(id+"F0.wireOp",EDGE,"E4.4.1")])],"isStart":true});
            var Q54;
            Q54=makeQuery(id+"F1.opExtrude","CAP_EDGE",EDGE,{"disambiguationData":[OSD([sQuery(id+"F0.wireOp",EDGE,"E0.1")])],"isStart":true});
            var Q55;
            Q55=makeQuery(id+"F1.opExtrude","CAP_EDGE",EDGE,{"disambiguationData":[OSD([sQuery(id+"F0.wireOp",EDGE,"E4.3.2")])],"isStart":true});
            var Q56;
            Q56=makeQuery(id+"F1.opExtrude","CAP_EDGE",EDGE,{"disambiguationData":[OSD([sQuery(id+"F0.wireOp",EDGE,"E6.3.0")])],"isStart":true});
            var Q57;
            Q57=makeQuery(id+"F1.opExtrude","CAP_EDGE",EDGE,{"disambiguationData":[OSD([sQuery(id+"F0.wireOp",EDGE,"E4.3.1")])],"isStart":true});
            var Q58;
            Q58=makeQuery(id+"F1.opExtrude","CAP_EDGE",EDGE,{"disambiguationData":[OSD([sQuery(id+"F0.wireOp",EDGE,"E0.2")])],"isStart":true});
            var Q59;
            {var subQ0=sQuery(id+"F2.wireOp",EDGE,"E11");Q59=makeQuery(id+"F3.boolean.opBoolean","INTERSECT",EDGE,{"derivedFrom":[makeQuery(id+"F1.opExtrude","CAP_FACE",FACE,{"disambiguationData":[OSD([sQuery(id+"F0.wireOp",EDGE,"E0.0"),sQuery(id+"F0.wireOp",EDGE,"E0.1"),sQuery(id+"F0.wireOp",EDGE,"E0.2"),sQuery(id+"F0.wireOp",EDGE,"E0.3"),sQuery(id+"F0.wireOp",EDGE,"E0.4"),sQuery(id+"F0.wireOp",EDGE,"E0.5"),sQuery(id+"F0.wireOp",EDGE,"E1.bottom"),sQuery(id+"F0.wireOp",EDGE,"E1.top"),sQuery(id+"F0.wireOp",EDGE,"E4.1.1"),sQuery(id+"F0.wireOp",EDGE,"E4.1.2"),sQuery(id+"F0.wireOp",EDGE,"E4.2.1"),sQuery(id+"F0.wireOp",EDGE,"E4.2.2"),sQuery(id+"F0.wireOp",EDGE,"E4.3.1"),sQuery(id+"F0.wireOp",EDGE,"E4.3.2"),sQuery(id+"F0.wireOp",EDGE,"E4.4.1"),sQuery(id+"F0.wireOp",EDGE,"E4.4.2"),sQuery(id+"F0.wireOp",EDGE,"E4.5.1"),sQuery(id+"F0.wireOp",EDGE,"E4.5.2"),sQuery(id+"F0.wireOp",EDGE,"E5"),sQuery(id+"F0.wireOp",EDGE,"E6.1.0"),sQuery(id+"F0.wireOp",EDGE,"E6.2.0"),sQuery(id+"F0.wireOp",EDGE,"E6.3.0"),sQuery(id+"F0.wireOp",EDGE,"E6.4.0"),sQuery(id+"F0.wireOp",EDGE,"E6.5.0")])],"isStart":true}),makeQuery(id+"F3.opExtrude","SWEPT_FACE",FACE,{"disambiguationData":[OSD([subQ0]),TDD([makeQuery(id+"F2.imprint","IMPRINT",EDGE,{"disambiguationData":[TD([[makeQuery(id+"F2.imprint","INTERSECT",VERTEX,{"derivedFrom":[subQ0,sQuery(id+"F2.wireOp",EDGE,"E17")]}),-1.0]])],"derivedFrom":subQ0})])]})]});}
            var Q60;
            {var subQ0=sQuery(id+"F2.wireOp",EDGE,"E12");Q60=makeQuery(id+"F3.boolean.opBoolean","INTERSECT",EDGE,{"derivedFrom":[makeQuery(id+"F1.opExtrude","CAP_FACE",FACE,{"disambiguationData":[OSD([sQuery(id+"F0.wireOp",EDGE,"E0.0"),sQuery(id+"F0.wireOp",EDGE,"E0.1"),sQuery(id+"F0.wireOp",EDGE,"E0.2"),sQuery(id+"F0.wireOp",EDGE,"E0.3"),sQuery(id+"F0.wireOp",EDGE,"E0.4"),sQuery(id+"F0.wireOp",EDGE,"E0.5"),sQuery(id+"F0.wireOp",EDGE,"E1.bottom"),sQuery(id+"F0.wireOp",EDGE,"E1.top"),sQuery(id+"F0.wireOp",EDGE,"E4.1.1"),sQuery(id+"F0.wireOp",EDGE,"E4.1.2"),sQuery(id+"F0.wireOp",EDGE,"E4.2.1"),sQuery(id+"F0.wireOp",EDGE,"E4.2.2"),sQuery(id+"F0.wireOp",EDGE,"E4.3.1"),sQuery(id+"F0.wireOp",EDGE,"E4.3.2"),sQuery(id+"F0.wireOp",EDGE,"E4.4.1"),sQuery(id+"F0.wireOp",EDGE,"E4.4.2"),sQuery(id+"F0.wireOp",EDGE,"E4.5.1"),sQuery(id+"F0.wireOp",EDGE,"E4.5.2"),sQuery(id+"F0.wireOp",EDGE,"E5"),sQuery(id+"F0.wireOp",EDGE,"E6.1.0"),sQuery(id+"F0.wireOp",EDGE,"E6.2.0"),sQuery(id+"F0.wireOp",EDGE,"E6.3.0"),sQuery(id+"F0.wireOp",EDGE,"E6.4.0"),sQuery(id+"F0.wireOp",EDGE,"E6.5.0")])],"isStart":true}),makeQuery(id+"F3.opExtrude","SWEPT_FACE",FACE,{"disambiguationData":[OSD([subQ0]),TDD([makeQuery(id+"F2.imprint","IMPRINT",EDGE,{"disambiguationData":[TD([[makeQuery(id+"F2.imprint","INTERSECT",VERTEX,{"derivedFrom":[subQ0,sQuery(id+"F2.wireOp",EDGE,"E18")]}),1.0]])],"derivedFrom":subQ0})])]})]});}
            var Q61;
            {var subQ0=sQuery(id+"F2.wireOp",EDGE,"E11");Q61=makeQuery(id+"F3.boolean.opBoolean","INTERSECT",EDGE,{"derivedFrom":[makeQuery(id+"F1.opExtrude","CAP_FACE",FACE,{"disambiguationData":[OSD([sQuery(id+"F0.wireOp",EDGE,"E0.0"),sQuery(id+"F0.wireOp",EDGE,"E0.1"),sQuery(id+"F0.wireOp",EDGE,"E0.2"),sQuery(id+"F0.wireOp",EDGE,"E0.3"),sQuery(id+"F0.wireOp",EDGE,"E0.4"),sQuery(id+"F0.wireOp",EDGE,"E0.5"),sQuery(id+"F0.wireOp",EDGE,"E1.bottom"),sQuery(id+"F0.wireOp",EDGE,"E1.top"),sQuery(id+"F0.wireOp",EDGE,"E4.1.1"),sQuery(id+"F0.wireOp",EDGE,"E4.1.2"),sQuery(id+"F0.wireOp",EDGE,"E4.2.1"),sQuery(id+"F0.wireOp",EDGE,"E4.2.2"),sQuery(id+"F0.wireOp",EDGE,"E4.3.1"),sQuery(id+"F0.wireOp",EDGE,"E4.3.2"),sQuery(id+"F0.wireOp",EDGE,"E4.4.1"),sQuery(id+"F0.wireOp",EDGE,"E4.4.2"),sQuery(id+"F0.wireOp",EDGE,"E4.5.1"),sQuery(id+"F0.wireOp",EDGE,"E4.5.2"),sQuery(id+"F0.wireOp",EDGE,"E5"),sQuery(id+"F0.wireOp",EDGE,"E6.1.0"),sQuery(id+"F0.wireOp",EDGE,"E6.2.0"),sQuery(id+"F0.wireOp",EDGE,"E6.3.0"),sQuery(id+"F0.wireOp",EDGE,"E6.4.0"),sQuery(id+"F0.wireOp",EDGE,"E6.5.0")])],"isStart":true}),makeQuery(id+"F3.opExtrude","SWEPT_FACE",FACE,{"disambiguationData":[OSD([subQ0]),TDD([makeQuery(id+"F2.imprint","IMPRINT",EDGE,{"disambiguationData":[TD([[makeQuery(id+"F2.imprint","INTERSECT",VERTEX,{"derivedFrom":[subQ0,sQuery(id+"F2.wireOp",EDGE,"E16")]}),1.0]])],"derivedFrom":subQ0})])]})]});}
            var Q62;
            {var subQ0=sQuery(id+"F2.wireOp",EDGE,"E10");Q62=makeQuery(id+"F3.boolean.opBoolean","INTERSECT",EDGE,{"derivedFrom":[makeQuery(id+"F1.opExtrude","CAP_FACE",FACE,{"disambiguationData":[OSD([sQuery(id+"F0.wireOp",EDGE,"E0.0"),sQuery(id+"F0.wireOp",EDGE,"E0.1"),sQuery(id+"F0.wireOp",EDGE,"E0.2"),sQuery(id+"F0.wireOp",EDGE,"E0.3"),sQuery(id+"F0.wireOp",EDGE,"E0.4"),sQuery(id+"F0.wireOp",EDGE,"E0.5"),sQuery(id+"F0.wireOp",EDGE,"E1.bottom"),sQuery(id+"F0.wireOp",EDGE,"E1.top"),sQuery(id+"F0.wireOp",EDGE,"E4.1.1"),sQuery(id+"F0.wireOp",EDGE,"E4.1.2"),sQuery(id+"F0.wireOp",EDGE,"E4.2.1"),sQuery(id+"F0.wireOp",EDGE,"E4.2.2"),sQuery(id+"F0.wireOp",EDGE,"E4.3.1"),sQuery(id+"F0.wireOp",EDGE,"E4.3.2"),sQuery(id+"F0.wireOp",EDGE,"E4.4.1"),sQuery(id+"F0.wireOp",EDGE,"E4.4.2"),sQuery(id+"F0.wireOp",EDGE,"E4.5.1"),sQuery(id+"F0.wireOp",EDGE,"E4.5.2"),sQuery(id+"F0.wireOp",EDGE,"E5"),sQuery(id+"F0.wireOp",EDGE,"E6.1.0"),sQuery(id+"F0.wireOp",EDGE,"E6.2.0"),sQuery(id+"F0.wireOp",EDGE,"E6.3.0"),sQuery(id+"F0.wireOp",EDGE,"E6.4.0"),sQuery(id+"F0.wireOp",EDGE,"E6.5.0")])],"isStart":true}),makeQuery(id+"F3.opExtrude","SWEPT_FACE",FACE,{"disambiguationData":[OSD([subQ0]),TDD([makeQuery(id+"F2.imprint","IMPRINT",EDGE,{"disambiguationData":[TD([[makeQuery(id+"F2.imprint","INTERSECT",VERTEX,{"derivedFrom":[subQ0,sQuery(id+"F2.wireOp",EDGE,"E13")]}),-1.0]])],"derivedFrom":subQ0})])]})]});}
            var Q63;
            {var subQ0=sQuery(id+"F2.wireOp",EDGE,"E9");Q63=makeQuery(id+"F3.boolean.opBoolean","INTERSECT",EDGE,{"derivedFrom":[makeQuery(id+"F1.opExtrude","CAP_FACE",FACE,{"disambiguationData":[OSD([sQuery(id+"F0.wireOp",EDGE,"E0.0"),sQuery(id+"F0.wireOp",EDGE,"E0.1"),sQuery(id+"F0.wireOp",EDGE,"E0.2"),sQuery(id+"F0.wireOp",EDGE,"E0.3"),sQuery(id+"F0.wireOp",EDGE,"E0.4"),sQuery(id+"F0.wireOp",EDGE,"E0.5"),sQuery(id+"F0.wireOp",EDGE,"E1.bottom"),sQuery(id+"F0.wireOp",EDGE,"E1.top"),sQuery(id+"F0.wireOp",EDGE,"E4.1.1"),sQuery(id+"F0.wireOp",EDGE,"E4.1.2"),sQuery(id+"F0.wireOp",EDGE,"E4.2.1"),sQuery(id+"F0.wireOp",EDGE,"E4.2.2"),sQuery(id+"F0.wireOp",EDGE,"E4.3.1"),sQuery(id+"F0.wireOp",EDGE,"E4.3.2"),sQuery(id+"F0.wireOp",EDGE,"E4.4.1"),sQuery(id+"F0.wireOp",EDGE,"E4.4.2"),sQuery(id+"F0.wireOp",EDGE,"E4.5.1"),sQuery(id+"F0.wireOp",EDGE,"E4.5.2"),sQuery(id+"F0.wireOp",EDGE,"E5"),sQuery(id+"F0.wireOp",EDGE,"E6.1.0"),sQuery(id+"F0.wireOp",EDGE,"E6.2.0"),sQuery(id+"F0.wireOp",EDGE,"E6.3.0"),sQuery(id+"F0.wireOp",EDGE,"E6.4.0"),sQuery(id+"F0.wireOp",EDGE,"E6.5.0")])],"isStart":true}),makeQuery(id+"F3.opExtrude","SWEPT_FACE",FACE,{"disambiguationData":[OSD([subQ0]),TDD([makeQuery(id+"F2.imprint","IMPRINT",EDGE,{"disambiguationData":[TD([[makeQuery(id+"F2.imprint","INTERSECT",VERTEX,{"derivedFrom":[subQ0,sQuery(id+"F2.wireOp",EDGE,"E15")]}),-1.0]])],"derivedFrom":subQ0})])]})]});}
            var Q64;
            {var subQ0=sQuery(id+"F2.wireOp",EDGE,"E10");Q64=makeQuery(id+"F3.boolean.opBoolean","INTERSECT",EDGE,{"derivedFrom":[makeQuery(id+"F1.opExtrude","CAP_FACE",FACE,{"disambiguationData":[OSD([sQuery(id+"F0.wireOp",EDGE,"E0.0"),sQuery(id+"F0.wireOp",EDGE,"E0.1"),sQuery(id+"F0.wireOp",EDGE,"E0.2"),sQuery(id+"F0.wireOp",EDGE,"E0.3"),sQuery(id+"F0.wireOp",EDGE,"E0.4"),sQuery(id+"F0.wireOp",EDGE,"E0.5"),sQuery(id+"F0.wireOp",EDGE,"E1.bottom"),sQuery(id+"F0.wireOp",EDGE,"E1.top"),sQuery(id+"F0.wireOp",EDGE,"E4.1.1"),sQuery(id+"F0.wireOp",EDGE,"E4.1.2"),sQuery(id+"F0.wireOp",EDGE,"E4.2.1"),sQuery(id+"F0.wireOp",EDGE,"E4.2.2"),sQuery(id+"F0.wireOp",EDGE,"E4.3.1"),sQuery(id+"F0.wireOp",EDGE,"E4.3.2"),sQuery(id+"F0.wireOp",EDGE,"E4.4.1"),sQuery(id+"F0.wireOp",EDGE,"E4.4.2"),sQuery(id+"F0.wireOp",EDGE,"E4.5.1"),sQuery(id+"F0.wireOp",EDGE,"E4.5.2"),sQuery(id+"F0.wireOp",EDGE,"E5"),sQuery(id+"F0.wireOp",EDGE,"E6.1.0"),sQuery(id+"F0.wireOp",EDGE,"E6.2.0"),sQuery(id+"F0.wireOp",EDGE,"E6.3.0"),sQuery(id+"F0.wireOp",EDGE,"E6.4.0"),sQuery(id+"F0.wireOp",EDGE,"E6.5.0")])],"isStart":true}),makeQuery(id+"F3.opExtrude","SWEPT_FACE",FACE,{"disambiguationData":[OSD([subQ0]),TDD([makeQuery(id+"F2.imprint","IMPRINT",EDGE,{"disambiguationData":[TD([[makeQuery(id+"F2.imprint","INTERSECT",VERTEX,{"derivedFrom":[subQ0,sQuery(id+"F2.wireOp",EDGE,"E14")]}),1.0]])],"derivedFrom":subQ0})])]})]});}
            var Q65;
            {var subQ0=sQuery(id+"F2.wireOp",EDGE,"E12");Q65=makeQuery(id+"F3.boolean.opBoolean","INTERSECT",EDGE,{"derivedFrom":[makeQuery(id+"F1.opExtrude","CAP_FACE",FACE,{"disambiguationData":[OSD([sQuery(id+"F0.wireOp",EDGE,"E0.0"),sQuery(id+"F0.wireOp",EDGE,"E0.1"),sQuery(id+"F0.wireOp",EDGE,"E0.2"),sQuery(id+"F0.wireOp",EDGE,"E0.3"),sQuery(id+"F0.wireOp",EDGE,"E0.4"),sQuery(id+"F0.wireOp",EDGE,"E0.5"),sQuery(id+"F0.wireOp",EDGE,"E1.bottom"),sQuery(id+"F0.wireOp",EDGE,"E1.top"),sQuery(id+"F0.wireOp",EDGE,"E4.1.1"),sQuery(id+"F0.wireOp",EDGE,"E4.1.2"),sQuery(id+"F0.wireOp",EDGE,"E4.2.1"),sQuery(id+"F0.wireOp",EDGE,"E4.2.2"),sQuery(id+"F0.wireOp",EDGE,"E4.3.1"),sQuery(id+"F0.wireOp",EDGE,"E4.3.2"),sQuery(id+"F0.wireOp",EDGE,"E4.4.1"),sQuery(id+"F0.wireOp",EDGE,"E4.4.2"),sQuery(id+"F0.wireOp",EDGE,"E4.5.1"),sQuery(id+"F0.wireOp",EDGE,"E4.5.2"),sQuery(id+"F0.wireOp",EDGE,"E5"),sQuery(id+"F0.wireOp",EDGE,"E6.1.0"),sQuery(id+"F0.wireOp",EDGE,"E6.2.0"),sQuery(id+"F0.wireOp",EDGE,"E6.3.0"),sQuery(id+"F0.wireOp",EDGE,"E6.4.0"),sQuery(id+"F0.wireOp",EDGE,"E6.5.0")])],"isStart":true}),makeQuery(id+"F3.opExtrude","SWEPT_FACE",FACE,{"disambiguationData":[OSD([subQ0]),TDD([makeQuery(id+"F2.imprint","IMPRINT",EDGE,{"disambiguationData":[TD([[makeQuery(id+"F2.imprint","INTERSECT",VERTEX,{"derivedFrom":[subQ0,sQuery(id+"F2.wireOp",EDGE,"E20")]}),-1.0]])],"derivedFrom":subQ0})])]})]});}
            var Q66;
            {var subQ0=sQuery(id+"F2.wireOp",EDGE,"E9");Q66=makeQuery(id+"F3.boolean.opBoolean","INTERSECT",EDGE,{"derivedFrom":[makeQuery(id+"F1.opExtrude","CAP_FACE",FACE,{"disambiguationData":[OSD([sQuery(id+"F0.wireOp",EDGE,"E0.0"),sQuery(id+"F0.wireOp",EDGE,"E0.1"),sQuery(id+"F0.wireOp",EDGE,"E0.2"),sQuery(id+"F0.wireOp",EDGE,"E0.3"),sQuery(id+"F0.wireOp",EDGE,"E0.4"),sQuery(id+"F0.wireOp",EDGE,"E0.5"),sQuery(id+"F0.wireOp",EDGE,"E1.bottom"),sQuery(id+"F0.wireOp",EDGE,"E1.top"),sQuery(id+"F0.wireOp",EDGE,"E4.1.1"),sQuery(id+"F0.wireOp",EDGE,"E4.1.2"),sQuery(id+"F0.wireOp",EDGE,"E4.2.1"),sQuery(id+"F0.wireOp",EDGE,"E4.2.2"),sQuery(id+"F0.wireOp",EDGE,"E4.3.1"),sQuery(id+"F0.wireOp",EDGE,"E4.3.2"),sQuery(id+"F0.wireOp",EDGE,"E4.4.1"),sQuery(id+"F0.wireOp",EDGE,"E4.4.2"),sQuery(id+"F0.wireOp",EDGE,"E4.5.1"),sQuery(id+"F0.wireOp",EDGE,"E4.5.2"),sQuery(id+"F0.wireOp",EDGE,"E5"),sQuery(id+"F0.wireOp",EDGE,"E6.1.0"),sQuery(id+"F0.wireOp",EDGE,"E6.2.0"),sQuery(id+"F0.wireOp",EDGE,"E6.3.0"),sQuery(id+"F0.wireOp",EDGE,"E6.4.0"),sQuery(id+"F0.wireOp",EDGE,"E6.5.0")])],"isStart":true}),makeQuery(id+"F3.opExtrude","SWEPT_FACE",FACE,{"disambiguationData":[OSD([subQ0]),TDD([makeQuery(id+"F2.imprint","IMPRINT",EDGE,{"disambiguationData":[TD([[makeQuery(id+"F2.imprint","INTERSECT",VERTEX,{"derivedFrom":[subQ0,sQuery(id+"F2.wireOp",EDGE,"E19")]}),1.0]])],"derivedFrom":subQ0})])]})]});}
            var Q67;
            {var subQ0=sQuery(id+"F2.wireOp",EDGE,"E8");Q67=makeQuery(id+"F3.boolean.opBoolean","INTERSECT",EDGE,{"derivedFrom":[makeQuery(id+"F1.opExtrude","CAP_FACE",FACE,{"disambiguationData":[OSD([sQuery(id+"F0.wireOp",EDGE,"E0.0"),sQuery(id+"F0.wireOp",EDGE,"E0.1"),sQuery(id+"F0.wireOp",EDGE,"E0.2"),sQuery(id+"F0.wireOp",EDGE,"E0.3"),sQuery(id+"F0.wireOp",EDGE,"E0.4"),sQuery(id+"F0.wireOp",EDGE,"E0.5"),sQuery(id+"F0.wireOp",EDGE,"E1.bottom"),sQuery(id+"F0.wireOp",EDGE,"E1.top"),sQuery(id+"F0.wireOp",EDGE,"E4.1.1"),sQuery(id+"F0.wireOp",EDGE,"E4.1.2"),sQuery(id+"F0.wireOp",EDGE,"E4.2.1"),sQuery(id+"F0.wireOp",EDGE,"E4.2.2"),sQuery(id+"F0.wireOp",EDGE,"E4.3.1"),sQuery(id+"F0.wireOp",EDGE,"E4.3.2"),sQuery(id+"F0.wireOp",EDGE,"E4.4.1"),sQuery(id+"F0.wireOp",EDGE,"E4.4.2"),sQuery(id+"F0.wireOp",EDGE,"E4.5.1"),sQuery(id+"F0.wireOp",EDGE,"E4.5.2"),sQuery(id+"F0.wireOp",EDGE,"E5"),sQuery(id+"F0.wireOp",EDGE,"E6.1.0"),sQuery(id+"F0.wireOp",EDGE,"E6.2.0"),sQuery(id+"F0.wireOp",EDGE,"E6.3.0"),sQuery(id+"F0.wireOp",EDGE,"E6.4.0"),sQuery(id+"F0.wireOp",EDGE,"E6.5.0")])],"isStart":true}),makeQuery(id+"F3.opExtrude","SWEPT_FACE",FACE,{"disambiguationData":[OSD([subQ0]),TDD([makeQuery(id+"F2.imprint","IMPRINT",EDGE,{"disambiguationData":[TD([[makeQuery(id+"F2.imprint","INTERSECT",VERTEX,{"disambiguationData":[OD(0.0)],"derivedFrom":[subQ0,sQuery(id+"F2.wireOp",EDGE,"E24")]}),1.0]])],"derivedFrom":subQ0})])]})]});}
            var Q68;
            {var subQ0=sQuery(id+"F2.wireOp",EDGE,"E8");Q68=makeQuery(id+"F3.boolean.opBoolean","INTERSECT",EDGE,{"derivedFrom":[makeQuery(id+"F1.opExtrude","CAP_FACE",FACE,{"disambiguationData":[OSD([sQuery(id+"F0.wireOp",EDGE,"E0.0"),sQuery(id+"F0.wireOp",EDGE,"E0.1"),sQuery(id+"F0.wireOp",EDGE,"E0.2"),sQuery(id+"F0.wireOp",EDGE,"E0.3"),sQuery(id+"F0.wireOp",EDGE,"E0.4"),sQuery(id+"F0.wireOp",EDGE,"E0.5"),sQuery(id+"F0.wireOp",EDGE,"E1.bottom"),sQuery(id+"F0.wireOp",EDGE,"E1.top"),sQuery(id+"F0.wireOp",EDGE,"E4.1.1"),sQuery(id+"F0.wireOp",EDGE,"E4.1.2"),sQuery(id+"F0.wireOp",EDGE,"E4.2.1"),sQuery(id+"F0.wireOp",EDGE,"E4.2.2"),sQuery(id+"F0.wireOp",EDGE,"E4.3.1"),sQuery(id+"F0.wireOp",EDGE,"E4.3.2"),sQuery(id+"F0.wireOp",EDGE,"E4.4.1"),sQuery(id+"F0.wireOp",EDGE,"E4.4.2"),sQuery(id+"F0.wireOp",EDGE,"E4.5.1"),sQuery(id+"F0.wireOp",EDGE,"E4.5.2"),sQuery(id+"F0.wireOp",EDGE,"E5"),sQuery(id+"F0.wireOp",EDGE,"E6.1.0"),sQuery(id+"F0.wireOp",EDGE,"E6.2.0"),sQuery(id+"F0.wireOp",EDGE,"E6.3.0"),sQuery(id+"F0.wireOp",EDGE,"E6.4.0"),sQuery(id+"F0.wireOp",EDGE,"E6.5.0")])],"isStart":true}),makeQuery(id+"F3.opExtrude","SWEPT_FACE",FACE,{"disambiguationData":[OSD([subQ0]),TDD([makeQuery(id+"F2.imprint","IMPRINT",EDGE,{"disambiguationData":[TD([[makeQuery(id+"F2.imprint","INTERSECT",VERTEX,{"disambiguationData":[OD(1.0)],"derivedFrom":[subQ0,sQuery(id+"F2.wireOp",EDGE,"E24")]}),-1.0]])],"derivedFrom":subQ0})])]})]});}
            var Q69;
            {var subQ0=sQuery(id+"F2.wireOp",EDGE,"E8");Q69=makeQuery(id+"F3.boolean.opBoolean","INTERSECT",EDGE,{"derivedFrom":[makeQuery(id+"F1.opExtrude","CAP_FACE",FACE,{"disambiguationData":[OSD([sQuery(id+"F0.wireOp",EDGE,"E0.0"),sQuery(id+"F0.wireOp",EDGE,"E0.1"),sQuery(id+"F0.wireOp",EDGE,"E0.2"),sQuery(id+"F0.wireOp",EDGE,"E0.3"),sQuery(id+"F0.wireOp",EDGE,"E0.4"),sQuery(id+"F0.wireOp",EDGE,"E0.5"),sQuery(id+"F0.wireOp",EDGE,"E1.bottom"),sQuery(id+"F0.wireOp",EDGE,"E1.top"),sQuery(id+"F0.wireOp",EDGE,"E4.1.1"),sQuery(id+"F0.wireOp",EDGE,"E4.1.2"),sQuery(id+"F0.wireOp",EDGE,"E4.2.1"),sQuery(id+"F0.wireOp",EDGE,"E4.2.2"),sQuery(id+"F0.wireOp",EDGE,"E4.3.1"),sQuery(id+"F0.wireOp",EDGE,"E4.3.2"),sQuery(id+"F0.wireOp",EDGE,"E4.4.1"),sQuery(id+"F0.wireOp",EDGE,"E4.4.2"),sQuery(id+"F0.wireOp",EDGE,"E4.5.1"),sQuery(id+"F0.wireOp",EDGE,"E4.5.2"),sQuery(id+"F0.wireOp",EDGE,"E5"),sQuery(id+"F0.wireOp",EDGE,"E6.1.0"),sQuery(id+"F0.wireOp",EDGE,"E6.2.0"),sQuery(id+"F0.wireOp",EDGE,"E6.3.0"),sQuery(id+"F0.wireOp",EDGE,"E6.4.0"),sQuery(id+"F0.wireOp",EDGE,"E6.5.0")])],"isStart":true}),makeQuery(id+"F3.opExtrude","SWEPT_FACE",FACE,{"disambiguationData":[OSD([subQ0]),TDD([makeQuery(id+"F2.imprint","IMPRINT",EDGE,{"disambiguationData":[TD([[makeQuery(id+"F2.imprint","INTERSECT",VERTEX,{"disambiguationData":[OD(1.0)],"derivedFrom":[subQ0,sQuery(id+"F2.wireOp",EDGE,"E23")]}),1.0]])],"derivedFrom":subQ0})])]})]});}
            var Q70;
            {var subQ0=sQuery(id+"F2.wireOp",EDGE,"E8");Q70=makeQuery(id+"F3.boolean.opBoolean","INTERSECT",EDGE,{"derivedFrom":[makeQuery(id+"F1.opExtrude","CAP_FACE",FACE,{"disambiguationData":[OSD([sQuery(id+"F0.wireOp",EDGE,"E0.0"),sQuery(id+"F0.wireOp",EDGE,"E0.1"),sQuery(id+"F0.wireOp",EDGE,"E0.2"),sQuery(id+"F0.wireOp",EDGE,"E0.3"),sQuery(id+"F0.wireOp",EDGE,"E0.4"),sQuery(id+"F0.wireOp",EDGE,"E0.5"),sQuery(id+"F0.wireOp",EDGE,"E1.bottom"),sQuery(id+"F0.wireOp",EDGE,"E1.top"),sQuery(id+"F0.wireOp",EDGE,"E4.1.1"),sQuery(id+"F0.wireOp",EDGE,"E4.1.2"),sQuery(id+"F0.wireOp",EDGE,"E4.2.1"),sQuery(id+"F0.wireOp",EDGE,"E4.2.2"),sQuery(id+"F0.wireOp",EDGE,"E4.3.1"),sQuery(id+"F0.wireOp",EDGE,"E4.3.2"),sQuery(id+"F0.wireOp",EDGE,"E4.4.1"),sQuery(id+"F0.wireOp",EDGE,"E4.4.2"),sQuery(id+"F0.wireOp",EDGE,"E4.5.1"),sQuery(id+"F0.wireOp",EDGE,"E4.5.2"),sQuery(id+"F0.wireOp",EDGE,"E5"),sQuery(id+"F0.wireOp",EDGE,"E6.1.0"),sQuery(id+"F0.wireOp",EDGE,"E6.2.0"),sQuery(id+"F0.wireOp",EDGE,"E6.3.0"),sQuery(id+"F0.wireOp",EDGE,"E6.4.0"),sQuery(id+"F0.wireOp",EDGE,"E6.5.0")])],"isStart":true}),makeQuery(id+"F3.opExtrude","SWEPT_FACE",FACE,{"disambiguationData":[OSD([subQ0]),TDD([makeQuery(id+"F2.imprint","IMPRINT",EDGE,{"disambiguationData":[TD([[makeQuery(id+"F2.imprint","INTERSECT",VERTEX,{"disambiguationData":[OD(0.0)],"derivedFrom":[subQ0,sQuery(id+"F2.wireOp",EDGE,"E23")]}),-1.0]])],"derivedFrom":subQ0})])]})]});}
            var Q71;
            {var subQ0=sQuery(id+"F2.wireOp",EDGE,"E10");Q71=makeQuery(id+"F3.boolean.opBoolean","COPY",EDGE,{"derivedFrom":makeQuery(id+"F3.opExtrude","CAP_EDGE",EDGE,{"disambiguationData":[OSD([subQ0]),TDD([makeQuery(id+"F2.imprint","IMPRINT",EDGE,{"disambiguationData":[TD([[makeQuery(id+"F2.imprint","INTERSECT",VERTEX,{"derivedFrom":[subQ0,sQuery(id+"F2.wireOp",EDGE,"E13")]}),-1.0]])],"derivedFrom":subQ0})])],"isStart":true})});}
            fillet(context, id + "F10", {"entities" : qUnion([Q0, Q1, Q2, Q3, Q4, Q5, Q6, Q7, Q8, Q9, Q10, Q11, Q12, Q13, Q14, Q15, Q16, Q17, Q18, Q19, Q20, Q21, Q22, Q23, Q24, Q25, Q26, Q27, Q28, Q29, Q30, Q31, Q32, Q33, Q34, Q35, Q36, Q37, Q38, Q39, Q40, Q41, Q42, Q43, Q44, Q45, Q46, Q47, Q48, Q49, Q50, Q51, Q52, Q53, Q54, Q55, Q56, Q57, Q58, Q59, Q60, Q61, Q62, Q63, Q64, Q65, Q66, Q67, Q68, Q69, Q70, Q71]), "radius" : 5 * mm, "tangentPropagation" : true, "allowEdgeOverflow" : false});
        }
    });
